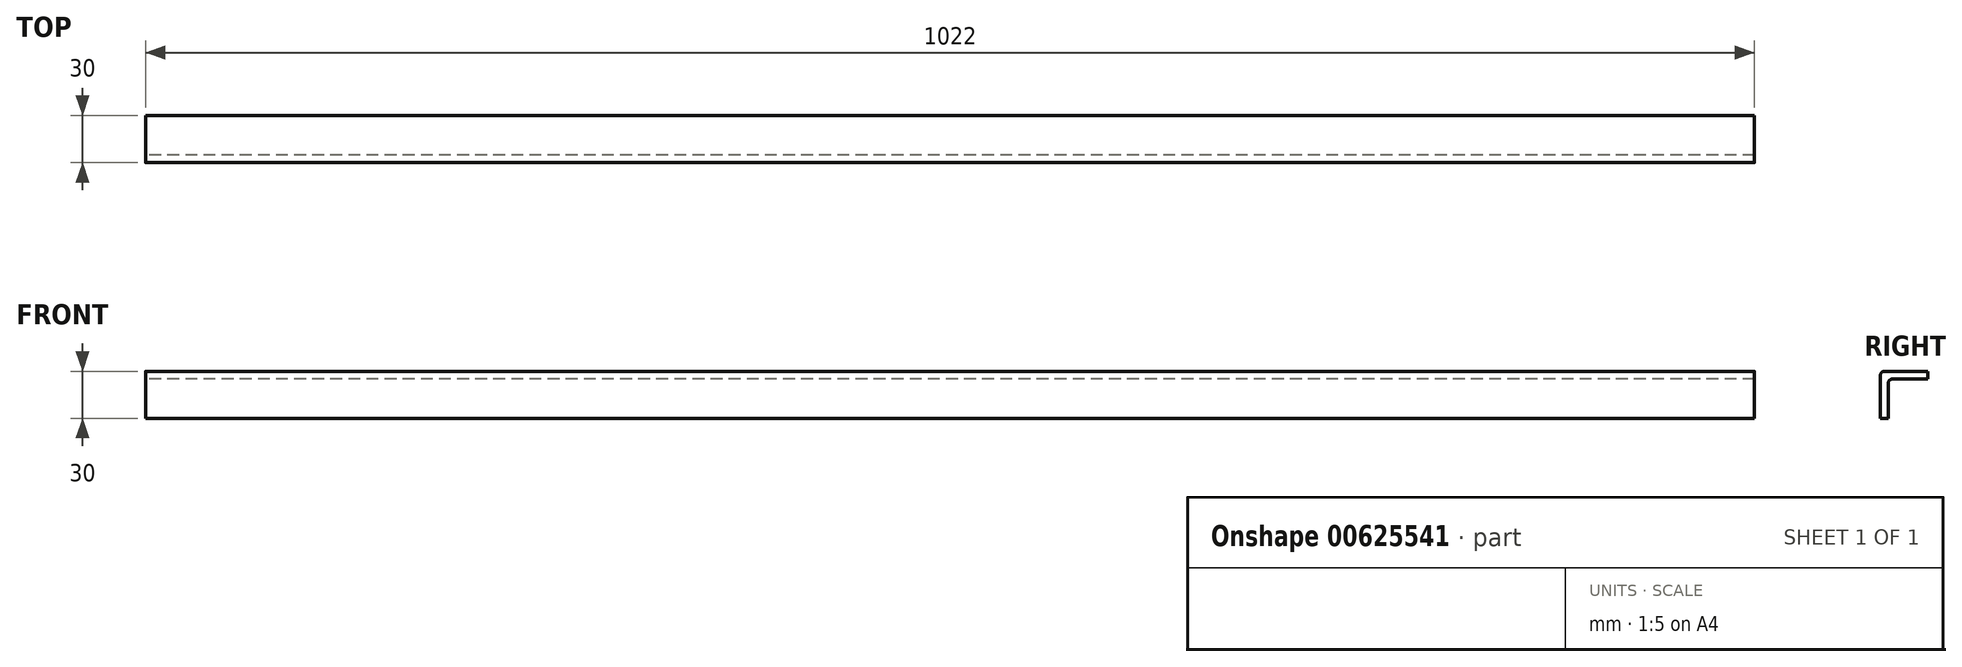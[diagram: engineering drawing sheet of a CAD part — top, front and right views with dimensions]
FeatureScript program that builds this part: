
annotation { "Feature Type Name" : "Feature", "Feature Type Description" : "" }
export const myFeature = defineFeature(function(context is Context, id is Id, definition is map)
    precondition{}
    {
        {
            var Q0;
            Q0=qCreatedBy(makeId("Right.planeOp"),FACE);
            var sketch = newSketch(context, id + "F0", { "sketchPlane" : qUnion([Q0])});
            skLineSegment(sketch, "E0.bottom", {"start": v(15, 15) * mm, "end": v(-12.5, 15) * mm});
            skLineSegment(sketch, "E0.top", {"start": v(-10, -15) * mm, "end": v(-15, -15) * mm});
            skLineSegment(sketch, "E0.left", {"start": v(15, 15) * mm, "end": v(15, 10) * mm});
            skLineSegment(sketch, "E0.right", {"start": v(-15, 12.5) * mm, "end": v(-15, -15) * mm});
            skPoint(sketch, "E0.middle", {"position": v(0, 0) * mm});
            skLineSegment(sketch, "E1", {"start": v(15, 10) * mm, "end": v(-7.5, 10) * mm});
            skLineSegment(sketch, "E2", {"start": v(-10, 7.5) * mm, "end": v(-10, -15) * mm});
            skPoint(sketch, "E3.visualSharp", {"position": v(-10, 10) * mm});
            skArc(sketch, "E3.filletArc", {"start": v(-7.5, 10) * mm, "mid": v(-9.27, 9.27) * mm, "end": v(-10, 7.5) * mm});
            skPoint(sketch, "E4.visualSharp", {"position": v(-15, 15) * mm});
            skArc(sketch, "E4.filletArc", {"start": v(-12.5, 15) * mm, "mid": v(-14.27, 14.27) * mm, "end": v(-15, 12.5) * mm});
            skPoint(sketch, "E5.orphan", {"position": v(15, -15) * mm});
            skSolve(sketch);
        }
        {
            var Q0;
            Q0=makeQuery(id+"F0.imprint","IMPRINT",FACE,{"disambiguationData":[TD([[makeQuery(id+"F0.imprint","IMPRINT",EDGE,{"derivedFrom":sQuery(id+"F0.wireOp",EDGE,"E0.bottom")}),1.0]])]});
            extrude(context, id + "F1", {"entities" : qUnion([Q0]), "depth" : 1022 * mm, "offsetDistance" : 25 * mm});
        }
    });
